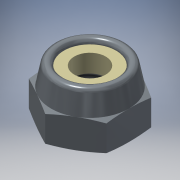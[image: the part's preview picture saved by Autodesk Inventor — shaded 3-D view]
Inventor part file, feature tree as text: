
AUTODESK INVENTOR PART (.ipt)
format: ipt  version: 2017.1 (Build 211199000, 199)  size: 224,768 bytes
history: native  units: mm (DEFAULTED — no unit token found)
features: sketch x5, extrude x2, revolve x2, other x1, plane x1, thread x1
ambient origin geometry x8: Origin, YZ Plane, XZ Plane, XY Plane, X Axis, Y Axis, Z Axis, Center Point
bodies: Solid1 (feature_tree)
feature tree (12):
  other  "Hexagon_flats_join1"
  extrude  "Extrusion1"  Depth=25.4mm TaperAngle=0.0deg
  revolve  "Revolution1"  Angle=90.0deg
  plane  "Work Plane1"
  extrude  "Extrusion2"  Depth=1.566333mm
  revolve  "Revolution2"  Angle=15.0deg
  thread  "Thread1"  [1 undecoded]
  sketch  "Sketch1"  dims[d0=9.525mm d3=25.4mm d4=0.0mm]
  sketch  "Sketch2"  dims[d5=13.788101mm d7=90.0deg]
  sketch  "Sketch3"  dims[d9=25.4mm d10=0.0mm d11=1.566333mm]
  sketch  "Sketch4"  dims[d12=15.0deg d13=15.0deg d14=9.525mm]
  sketch  "Sketch5"  dims[d15=90.0deg d16=25.4mm d17=0.0mm]
note: 1 required parameter value undecoded (feature->parameter linkage not recoverable at this tier; creation-order binding heuristic only, values carry confidence <= 0.55)
